annotation { "Feature Type Name" : "Feature", "Feature Type Description" : "" }
export const myFeature = defineFeature(function(context is Context, id is Id, definition is map)
    precondition{}
    {
        {
            var Q0;
            Q0=qCreatedBy(makeId("Top.planeOp"),FACE);
            var sketch = newSketch(context, id + "F0", { "sketchPlane" : qUnion([Q0])});
            skLineSegment(sketch, "E0.bottom", {"start": v(-41.2, 53) * mm, "end": v(24.8, 53) * mm});
            skLineSegment(sketch, "E0.top", {"start": v(-41.2, 0) * mm, "end": v(24.8, 0) * mm});
            skLineSegment(sketch, "E0.left", {"start": v(-44.2, 48.01) * mm, "end": v(-44.2, 15.01) * mm});
            skLineSegment(sketch, "E0.right", {"start": v(24.8, 53) * mm, "end": v(24.8, 0) * mm});
            skCircle(sketch, "E1", {"center": v(9.8, 2.5) * mm, "radius": 1.5 * mm});
            skCircle(sketch, "E2", {"center": v(9.8, 50.5) * mm, "radius": 1.5 * mm});
            skLineSegment(sketch, "E3", {"start": v(-41.2, 53) * mm, "end": v(-41.2, 50) * mm});
            skLineSegment(sketch, "E4", {"start": v(-41.2, 50) * mm, "end": v(-44.2, 48.01) * mm});
            skLineSegment(sketch, "E5", {"start": v(-44.2, 15.01) * mm, "end": v(-41.2, 13) * mm});
            skPoint(sketch, "E6.orphan", {"position": v(-44.2, 53) * mm});
            skLineSegment(sketch, "E7", {"start": v(-41.2, 12.57) * mm, "end": v(-41.2, 0) * mm});
            skPoint(sketch, "E8.orphan", {"position": v(-41.2, 0) * mm});
            skLineSegment(sketch, "E9.trimOffspring", {"start": v(-41.2, 13) * mm, "end": v(-41.2, 12.57) * mm});
            skCircle(sketch, "E10", {"center": v(-41.7, 17.47) * mm, "radius": 1.5 * mm});
            skPoint(sketch, "E11.centerSnap0", {"position": v(-41.2, 51.5) * mm});
            skLineSegment(sketch, "E12", {"start": v(-41.7, 17.47) * mm, "end": v(-41.7, 18.97) * mm});
            skLineSegment(sketch, "E13", {"start": v(-41.2, 47) * mm, "end": v(-41.2, 50) * mm});
            skCircle(sketch, "E14", {"center": v(-41.7, 45.53) * mm, "radius": 1.5 * mm});
            skLineSegment(sketch, "E15.bottom", {"start": v(13.3, 12) * mm, "end": v(27.3, 12) * mm});
            skLineSegment(sketch, "E15.top", {"start": v(13.3, 3) * mm, "end": v(27.3, 3) * mm});
            skLineSegment(sketch, "E15.left", {"start": v(13.3, 12) * mm, "end": v(13.3, 3) * mm});
            skLineSegment(sketch, "E15.right", {"start": v(27.3, 12) * mm, "end": v(27.3, 3) * mm});
            skSolve(sketch);
        }
        {
            var Q0;
            Q0=makeQuery(id+"F0.imprint","IMPRINT",FACE,{"disambiguationData":[TD([[makeQuery(id+"F0.imprint","IMPRINT",EDGE,{"derivedFrom":sQuery(id+"F0.wireOp",EDGE,"E0.bottom")}),-1.0]])]});
            var Q1;
            {var subQ5=sQuery(id+"F0.wireOp",EDGE,"E15.left");Q1=makeQuery(id+"F0.imprint","IMPRINT",FACE,{"disambiguationData":[TD([[makeQuery(id+"F0.imprint","IMPRINT",EDGE,{"derivedFrom":subQ5}),1.0]])]});}
            extrude(context, id + "F1", {"entities" : qUnion([Q0, Q1]), "depth" : 1.5 * mm});
        }
        {
            var Q0;
            Q0=makeQuery(id+"F1.opExtrude","CAP_FACE",FACE,{"disambiguationData":[OSD([sQuery(id+"F0.wireOp",EDGE,"E0.bottom"),sQuery(id+"F0.wireOp",EDGE,"E0.top"),sQuery(id+"F0.wireOp",EDGE,"E0.left"),sQuery(id+"F0.wireOp",EDGE,"E0.right"),sQuery(id+"F0.wireOp",EDGE,"E1"),sQuery(id+"F0.wireOp",EDGE,"E2"),sQuery(id+"F0.wireOp",EDGE,"E3"),sQuery(id+"F0.wireOp",EDGE,"E4"),sQuery(id+"F0.wireOp",EDGE,"E5"),sQuery(id+"F0.wireOp",EDGE,"E7"),sQuery(id+"F0.wireOp",EDGE,"E9.trimOffspring")])],"isStart":false});
            var sketch = newSketch(context, id + "F2", { "sketchPlane" : qUnion([Q0])});
            skLineSegment(sketch, "E16.bottom", {"start": v(-18.2, 51.5) * mm, "end": v(2.8, 51.5) * mm});
            skLineSegment(sketch, "E16.left", {"start": v(-18.2, 51.5) * mm, "end": v(-18.2, 49.5) * mm});
            skLineSegment(sketch, "E16.right", {"start": v(2.8, 51.5) * mm, "end": v(2.8, 49.5) * mm});
            skLineSegment(sketch, "E17", {"start": v(-18.2, 49.5) * mm, "end": v(2.8, 49.5) * mm});
            skLineSegment(sketch, "E18.bottom", {"start": v(-19.2, 49.5) * mm, "end": v(-40.2, 49.5) * mm});
            skLineSegment(sketch, "E18.top", {"start": v(-19.2, 51.5) * mm, "end": v(-40.2, 51.5) * mm});
            skLineSegment(sketch, "E18.left", {"start": v(-19.2, 49.5) * mm, "end": v(-19.2, 51.5) * mm});
            skLineSegment(sketch, "E18.right", {"start": v(-40.2, 49.5) * mm, "end": v(-40.2, 51.5) * mm});
            skLineSegment(sketch, "E19.bottom", {"start": v(-6.2, 1) * mm, "end": v(-22.2, 1) * mm});
            skLineSegment(sketch, "E19.top", {"start": v(-6.2, 3) * mm, "end": v(-22.2, 3) * mm});
            skLineSegment(sketch, "E19.left", {"start": v(-6.2, 1) * mm, "end": v(-6.2, 3) * mm});
            skLineSegment(sketch, "E19.right", {"start": v(-22.2, 1) * mm, "end": v(-22.2, 3) * mm});
            skLineSegment(sketch, "E20.bottom", {"start": v(-24.2, 1) * mm, "end": v(-40.2, 1) * mm});
            skLineSegment(sketch, "E20.top", {"start": v(-24.2, 3) * mm, "end": v(-40.2, 3) * mm});
            skLineSegment(sketch, "E20.left", {"start": v(-24.2, 1) * mm, "end": v(-24.2, 3) * mm});
            skLineSegment(sketch, "E20.right", {"start": v(-41.2, 1) * mm, "end": v(-41.2, 3) * mm});
            skLineSegment(sketch, "E21", {"start": v(-40.2, 3) * mm, "end": v(-40.2, 1) * mm});
            skSolve(sketch);
        }
        {
            var Q0;
            Q0 = qSketchRegion(id + "F2", true);
            extrude(context, id + "F3", {"entities" : qUnion([Q0]), "operationType" : NewBodyOperationType.ADD, "depth" : 9 * mm});
        }
        {
            var Q0;
            Q0=makeQuery(id+"F3.opExtrude","CAP_FACE",FACE,{"disambiguationData":[OSD([sQuery(id+"F2.wireOp",EDGE,"E18.bottom"),sQuery(id+"F2.wireOp",EDGE,"E18.top"),sQuery(id+"F2.wireOp",EDGE,"E18.left"),sQuery(id+"F2.wireOp",EDGE,"E18.right")])],"isStart":false});
            var sketch = newSketch(context, id + "F4", { "sketchPlane" : qUnion([Q0])});
            skLineSegment(sketch, "E22.bottom", {"start": v(-39.2, 51.25) * mm, "end": v(-37.7, 51.25) * mm});
            skLineSegment(sketch, "E22.top", {"start": v(-39.2, 49.75) * mm, "end": v(-37.7, 49.75) * mm});
            skLineSegment(sketch, "E22.left", {"start": v(-39.2, 51.25) * mm, "end": v(-39.2, 49.75) * mm});
            skLineSegment(sketch, "E22.right", {"start": v(-37.7, 51.25) * mm, "end": v(-37.7, 49.75) * mm});
            skLineSegment(sketch, "E23.bottom", {"start": v(-36.7, 51.25) * mm, "end": v(-35.2, 51.25) * mm});
            skLineSegment(sketch, "E23.top", {"start": v(-36.7, 49.75) * mm, "end": v(-35.2, 49.75) * mm});
            skLineSegment(sketch, "E23.left", {"start": v(-36.7, 51.25) * mm, "end": v(-36.7, 49.75) * mm});
            skLineSegment(sketch, "E23.right", {"start": v(-35.2, 51.25) * mm, "end": v(-35.2, 49.75) * mm});
            skLineSegment(sketch, "E24.bottom", {"start": v(-34.2, 51.25) * mm, "end": v(-32.7, 51.25) * mm});
            skLineSegment(sketch, "E24.top", {"start": v(-34.2, 49.75) * mm, "end": v(-32.7, 49.75) * mm});
            skLineSegment(sketch, "E24.left", {"start": v(-34.2, 51.25) * mm, "end": v(-34.2, 49.75) * mm});
            skLineSegment(sketch, "E24.right", {"start": v(-32.7, 51.25) * mm, "end": v(-32.7, 49.75) * mm});
            skLineSegment(sketch, "E25.bottom", {"start": v(-31.7, 51.25) * mm, "end": v(-30.2, 51.25) * mm});
            skLineSegment(sketch, "E25.top", {"start": v(-31.7, 49.75) * mm, "end": v(-30.2, 49.75) * mm});
            skLineSegment(sketch, "E25.left", {"start": v(-31.7, 51.25) * mm, "end": v(-31.7, 49.75) * mm});
            skLineSegment(sketch, "E25.right", {"start": v(-30.2, 51.25) * mm, "end": v(-30.2, 49.75) * mm});
            skLineSegment(sketch, "E26.bottom", {"start": v(-29.2, 51.25) * mm, "end": v(-27.7, 51.25) * mm});
            skLineSegment(sketch, "E26.top", {"start": v(-29.2, 49.75) * mm, "end": v(-27.7, 49.75) * mm});
            skLineSegment(sketch, "E26.left", {"start": v(-29.2, 51.25) * mm, "end": v(-29.2, 49.75) * mm});
            skLineSegment(sketch, "E26.right", {"start": v(-27.7, 51.25) * mm, "end": v(-27.7, 49.75) * mm});
            skLineSegment(sketch, "E27.bottom", {"start": v(-26.7, 51.25) * mm, "end": v(-25.2, 51.25) * mm});
            skLineSegment(sketch, "E27.top", {"start": v(-26.7, 49.75) * mm, "end": v(-25.2, 49.75) * mm});
            skLineSegment(sketch, "E27.left", {"start": v(-26.7, 51.25) * mm, "end": v(-26.7, 49.75) * mm});
            skLineSegment(sketch, "E27.right", {"start": v(-25.2, 51.25) * mm, "end": v(-25.2, 49.75) * mm});
            skLineSegment(sketch, "E28.right", {"start": v(124.56, 51.25) * mm, "end": v(124.56, 49.75) * mm});
            skLineSegment(sketch, "E29.bottom", {"start": v(-21.7, 51.25) * mm, "end": v(-20.2, 51.25) * mm});
            skLineSegment(sketch, "E29.top", {"start": v(-21.7, 49.75) * mm, "end": v(-20.2, 49.75) * mm});
            skLineSegment(sketch, "E29.left", {"start": v(-21.7, 51.25) * mm, "end": v(-21.7, 49.75) * mm});
            skLineSegment(sketch, "E29.right", {"start": v(-20.2, 51.25) * mm, "end": v(-20.2, 49.75) * mm});
            skLineSegment(sketch, "E30.bottom", {"start": v(-24.2, 51.25) * mm, "end": v(-22.7, 51.25) * mm});
            skLineSegment(sketch, "E30.top", {"start": v(-24.2, 49.75) * mm, "end": v(-22.7, 49.75) * mm});
            skLineSegment(sketch, "E30.left", {"start": v(-24.2, 51.25) * mm, "end": v(-24.2, 49.75) * mm});
            skLineSegment(sketch, "E30.right", {"start": v(-22.7, 51.25) * mm, "end": v(-22.7, 49.75) * mm});
            skSolve(sketch);
        }
        {
            var Q0;
            Q0 = qSketchRegion(id + "F4", true);
            extrude(context, id + "F5", {"entities" : qUnion([Q0]), "operationType" : NewBodyOperationType.REMOVE, "oppositeDirection" : true, "depth" : 6 * mm});
        }
        {
            var Q0;
            Q0=makeQuery(id+"F3.opExtrude","CAP_FACE",FACE,{"disambiguationData":[OSD([sQuery(id+"F2.wireOp",EDGE,"E16.bottom"),sQuery(id+"F2.wireOp",EDGE,"E16.left"),sQuery(id+"F2.wireOp",EDGE,"E16.right"),sQuery(id+"F2.wireOp",EDGE,"E17")])],"isStart":false});
            var sketch = newSketch(context, id + "F6", { "sketchPlane" : qUnion([Q0])});
            skLineSegment(sketch, "E31.bottom", {"start": v(-17.2, 51.25) * mm, "end": v(-15.7, 51.25) * mm});
            skLineSegment(sketch, "E31.top", {"start": v(-17.2, 49.75) * mm, "end": v(-15.7, 49.75) * mm});
            skLineSegment(sketch, "E31.left", {"start": v(-17.2, 51.25) * mm, "end": v(-17.2, 49.75) * mm});
            skLineSegment(sketch, "E31.right", {"start": v(-15.7, 51.25) * mm, "end": v(-15.7, 49.75) * mm});
            skLineSegment(sketch, "E32.bottom", {"start": v(-14.7, 51.25) * mm, "end": v(-13.2, 51.25) * mm});
            skLineSegment(sketch, "E32.top", {"start": v(-14.7, 49.75) * mm, "end": v(-13.2, 49.75) * mm});
            skLineSegment(sketch, "E32.left", {"start": v(-14.7, 51.25) * mm, "end": v(-14.7, 49.75) * mm});
            skLineSegment(sketch, "E32.right", {"start": v(-13.2, 51.25) * mm, "end": v(-13.2, 49.75) * mm});
            skLineSegment(sketch, "E33.bottom", {"start": v(-12.2, 51.25) * mm, "end": v(-10.7, 51.25) * mm});
            skLineSegment(sketch, "E33.top", {"start": v(-12.2, 49.75) * mm, "end": v(-10.7, 49.75) * mm});
            skLineSegment(sketch, "E33.left", {"start": v(-12.2, 51.25) * mm, "end": v(-12.2, 49.75) * mm});
            skLineSegment(sketch, "E33.right", {"start": v(-10.7, 51.25) * mm, "end": v(-10.7, 49.75) * mm});
            skLineSegment(sketch, "E34.bottom", {"start": v(-9.7, 51.25) * mm, "end": v(-8.2, 51.25) * mm});
            skLineSegment(sketch, "E34.top", {"start": v(-9.7, 49.75) * mm, "end": v(-8.2, 49.75) * mm});
            skLineSegment(sketch, "E34.left", {"start": v(-9.7, 51.25) * mm, "end": v(-9.7, 49.75) * mm});
            skLineSegment(sketch, "E34.right", {"start": v(-8.2, 51.25) * mm, "end": v(-8.2, 49.75) * mm});
            skLineSegment(sketch, "E35.bottom", {"start": v(-7.2, 51.25) * mm, "end": v(-5.7, 51.25) * mm});
            skLineSegment(sketch, "E35.top", {"start": v(-7.2, 49.75) * mm, "end": v(-5.7, 49.75) * mm});
            skLineSegment(sketch, "E35.left", {"start": v(-7.2, 51.25) * mm, "end": v(-7.2, 49.75) * mm});
            skLineSegment(sketch, "E35.right", {"start": v(-5.7, 51.25) * mm, "end": v(-5.7, 49.75) * mm});
            skLineSegment(sketch, "E36.bottom", {"start": v(-4.7, 51.25) * mm, "end": v(-3.2, 51.25) * mm});
            skLineSegment(sketch, "E36.top", {"start": v(-4.7, 49.75) * mm, "end": v(-3.2, 49.75) * mm});
            skLineSegment(sketch, "E36.left", {"start": v(-4.7, 51.25) * mm, "end": v(-4.7, 49.75) * mm});
            skLineSegment(sketch, "E36.right", {"start": v(-3.2, 51.25) * mm, "end": v(-3.2, 49.75) * mm});
            skLineSegment(sketch, "E37.right", {"start": v(137.9, 51.25) * mm, "end": v(137.9, 49.75) * mm});
            skLineSegment(sketch, "E38.bottom", {"start": v(0.3, 51.25) * mm, "end": v(1.8, 51.25) * mm});
            skLineSegment(sketch, "E38.top", {"start": v(0.3, 49.75) * mm, "end": v(1.8, 49.75) * mm});
            skLineSegment(sketch, "E38.left", {"start": v(0.3, 51.25) * mm, "end": v(0.3, 49.75) * mm});
            skLineSegment(sketch, "E38.right", {"start": v(1.8, 51.25) * mm, "end": v(1.8, 49.75) * mm});
            skLineSegment(sketch, "E39.bottom", {"start": v(-2.2, 51.25) * mm, "end": v(-0.7, 51.25) * mm});
            skLineSegment(sketch, "E39.top", {"start": v(-2.2, 49.75) * mm, "end": v(-0.7, 49.75) * mm});
            skLineSegment(sketch, "E39.left", {"start": v(-2.2, 51.25) * mm, "end": v(-2.2, 49.75) * mm});
            skLineSegment(sketch, "E39.right", {"start": v(-0.7, 51.25) * mm, "end": v(-0.7, 49.75) * mm});
            skSolve(sketch);
        }
        {
            var Q0;
            Q0=makeQuery(id+"F6.imprint","IMPRINT",FACE,{"disambiguationData":[TD([[makeQuery(id+"F6.imprint","IMPRINT",EDGE,{"derivedFrom":sQuery(id+"F6.wireOp",EDGE,"E32.bottom")}),-1.0]])]});
            var Q1;
            Q1=makeQuery(id+"F6.imprint","IMPRINT",FACE,{"disambiguationData":[TD([[makeQuery(id+"F6.imprint","IMPRINT",EDGE,{"derivedFrom":sQuery(id+"F6.wireOp",EDGE,"E33.bottom")}),-1.0]])]});
            var Q2;
            Q2=makeQuery(id+"F6.imprint","IMPRINT",FACE,{"disambiguationData":[TD([[makeQuery(id+"F6.imprint","IMPRINT",EDGE,{"derivedFrom":sQuery(id+"F6.wireOp",EDGE,"E34.bottom")}),-1.0]])]});
            var Q3;
            Q3=makeQuery(id+"F6.imprint","IMPRINT",FACE,{"disambiguationData":[TD([[makeQuery(id+"F6.imprint","IMPRINT",EDGE,{"derivedFrom":sQuery(id+"F6.wireOp",EDGE,"E35.bottom")}),-1.0]])]});
            var Q4;
            Q4=makeQuery(id+"F6.imprint","IMPRINT",FACE,{"disambiguationData":[TD([[makeQuery(id+"F6.imprint","IMPRINT",EDGE,{"derivedFrom":sQuery(id+"F6.wireOp",EDGE,"E36.bottom")}),-1.0]])]});
            var Q5;
            Q5=makeQuery(id+"F6.imprint","IMPRINT",FACE,{"disambiguationData":[TD([[makeQuery(id+"F6.imprint","IMPRINT",EDGE,{"derivedFrom":sQuery(id+"F6.wireOp",EDGE,"E38.bottom")}),-1.0]])]});
            var Q6;
            Q6=makeQuery(id+"F6.imprint","IMPRINT",FACE,{"disambiguationData":[TD([[makeQuery(id+"F6.imprint","IMPRINT",EDGE,{"derivedFrom":sQuery(id+"F6.wireOp",EDGE,"E39.bottom")}),-1.0]])]});
            var Q7;
            Q7=makeQuery(id+"F6.imprint","IMPRINT",FACE,{"disambiguationData":[TD([[makeQuery(id+"F6.imprint","IMPRINT",EDGE,{"derivedFrom":sQuery(id+"F6.wireOp",EDGE,"E31.bottom")}),-1.0]])]});
            var Q8;
            Q8=makeQuery(id+"F6.imprint","IMPRINT",FACE,{"disambiguationData":[TD([[makeQuery(id+"F6.imprint","IMPRINT",EDGE,{"derivedFrom":sQuery(id+"F6.wireOp",EDGE,"E32.bottom")}),-1.0]])]});
            var Q9;
            Q9=makeQuery(id+"F6.imprint","IMPRINT",FACE,{"disambiguationData":[TD([[makeQuery(id+"F6.imprint","IMPRINT",EDGE,{"derivedFrom":sQuery(id+"F6.wireOp",EDGE,"E33.bottom")}),-1.0]])]});
            var Q10;
            Q10=makeQuery(id+"F6.imprint","IMPRINT",FACE,{"disambiguationData":[TD([[makeQuery(id+"F6.imprint","IMPRINT",EDGE,{"derivedFrom":sQuery(id+"F6.wireOp",EDGE,"E34.bottom")}),-1.0]])]});
            var Q11;
            Q11=makeQuery(id+"F6.imprint","IMPRINT",FACE,{"disambiguationData":[TD([[makeQuery(id+"F6.imprint","IMPRINT",EDGE,{"derivedFrom":sQuery(id+"F6.wireOp",EDGE,"E35.bottom")}),-1.0]])]});
            var Q12;
            Q12=makeQuery(id+"F6.imprint","IMPRINT",FACE,{"disambiguationData":[TD([[makeQuery(id+"F6.imprint","IMPRINT",EDGE,{"derivedFrom":sQuery(id+"F6.wireOp",EDGE,"E36.bottom")}),-1.0]])]});
            var Q13;
            Q13=makeQuery(id+"F6.imprint","IMPRINT",FACE,{"disambiguationData":[TD([[makeQuery(id+"F6.imprint","IMPRINT",EDGE,{"derivedFrom":sQuery(id+"F6.wireOp",EDGE,"E38.bottom")}),-1.0]])]});
            var Q14;
            Q14=makeQuery(id+"F6.imprint","IMPRINT",FACE,{"disambiguationData":[TD([[makeQuery(id+"F6.imprint","IMPRINT",EDGE,{"derivedFrom":sQuery(id+"F6.wireOp",EDGE,"E39.bottom")}),-1.0]])]});
            extrude(context, id + "F7", {"entities" : qUnion([Q0, Q1, Q2, Q3, Q4, Q5, Q6, Q7, Q8, Q9, Q10, Q11, Q12, Q13, Q14]), "operationType" : NewBodyOperationType.REMOVE, "oppositeDirection" : true, "depth" : 6 * mm});
        }
        {
            var Q0;
            Q0=makeQuery(id+"F3.opExtrude","CAP_FACE",FACE,{"disambiguationData":[OSD([sQuery(id+"F2.wireOp",EDGE,"E20.bottom"),sQuery(id+"F2.wireOp",EDGE,"E20.top"),sQuery(id+"F2.wireOp",EDGE,"E20.left"),sQuery(id+"F2.wireOp",EDGE,"E21")])],"isStart":false});
            var sketch = newSketch(context, id + "F8", { "sketchPlane" : qUnion([Q0])});
            skLineSegment(sketch, "E40.bottom", {"start": v(-39.2, 2.75) * mm, "end": v(-37.7, 2.75) * mm});
            skLineSegment(sketch, "E40.top", {"start": v(-39.2, 1.25) * mm, "end": v(-37.7, 1.25) * mm});
            skLineSegment(sketch, "E40.left", {"start": v(-39.2, 2.75) * mm, "end": v(-39.2, 1.25) * mm});
            skLineSegment(sketch, "E40.right", {"start": v(-37.7, 2.75) * mm, "end": v(-37.7, 1.25) * mm});
            skLineSegment(sketch, "E41.bottom", {"start": v(-36.7, 2.75) * mm, "end": v(-35.2, 2.75) * mm});
            skLineSegment(sketch, "E41.top", {"start": v(-36.7, 1.25) * mm, "end": v(-35.2, 1.25) * mm});
            skLineSegment(sketch, "E41.left", {"start": v(-36.7, 2.75) * mm, "end": v(-36.7, 1.25) * mm});
            skLineSegment(sketch, "E41.right", {"start": v(-35.2, 2.75) * mm, "end": v(-35.2, 1.25) * mm});
            skLineSegment(sketch, "E42.bottom", {"start": v(-34.2, 2.75) * mm, "end": v(-32.7, 2.75) * mm});
            skLineSegment(sketch, "E42.top", {"start": v(-34.2, 1.25) * mm, "end": v(-32.7, 1.25) * mm});
            skLineSegment(sketch, "E42.left", {"start": v(-34.2, 2.75) * mm, "end": v(-34.2, 1.25) * mm});
            skLineSegment(sketch, "E42.right", {"start": v(-32.7, 2.75) * mm, "end": v(-32.7, 1.25) * mm});
            skLineSegment(sketch, "E43.bottom", {"start": v(-31.7, 2.75) * mm, "end": v(-30.2, 2.75) * mm});
            skLineSegment(sketch, "E43.top", {"start": v(-31.7, 1.25) * mm, "end": v(-30.2, 1.25) * mm});
            skLineSegment(sketch, "E43.left", {"start": v(-31.7, 2.75) * mm, "end": v(-31.7, 1.25) * mm});
            skLineSegment(sketch, "E43.right", {"start": v(-30.2, 2.75) * mm, "end": v(-30.2, 1.25) * mm});
            skLineSegment(sketch, "E44.bottom", {"start": v(-29.2, 2.75) * mm, "end": v(-27.7, 2.75) * mm});
            skLineSegment(sketch, "E44.top", {"start": v(-29.2, 1.25) * mm, "end": v(-27.7, 1.25) * mm});
            skLineSegment(sketch, "E44.left", {"start": v(-29.2, 2.75) * mm, "end": v(-29.2, 1.25) * mm});
            skLineSegment(sketch, "E44.right", {"start": v(-27.7, 2.75) * mm, "end": v(-27.7, 1.25) * mm});
            skLineSegment(sketch, "E45.bottom", {"start": v(-26.7, 2.75) * mm, "end": v(-25.2, 2.75) * mm});
            skLineSegment(sketch, "E45.top", {"start": v(-26.7, 1.25) * mm, "end": v(-25.2, 1.25) * mm});
            skLineSegment(sketch, "E45.left", {"start": v(-26.7, 2.75) * mm, "end": v(-26.7, 1.25) * mm});
            skLineSegment(sketch, "E45.right", {"start": v(-25.2, 2.75) * mm, "end": v(-25.2, 1.25) * mm});
            skLineSegment(sketch, "E46.right", {"start": v(102.2, 2.75) * mm, "end": v(102.2, 1.25) * mm});
            skSolve(sketch);
        }
        {
            var Q0;
            Q0 = qSketchRegion(id + "F8", true);
            extrude(context, id + "F9", {"entities" : qUnion([Q0]), "operationType" : NewBodyOperationType.REMOVE, "oppositeDirection" : true, "depth" : 6 * mm});
        }
        {
            var Q0;
            Q0=makeQuery(id+"F3.opExtrude","CAP_FACE",FACE,{"disambiguationData":[OSD([sQuery(id+"F2.wireOp",EDGE,"E19.bottom"),sQuery(id+"F2.wireOp",EDGE,"E19.top"),sQuery(id+"F2.wireOp",EDGE,"E19.left"),sQuery(id+"F2.wireOp",EDGE,"E19.right")])],"isStart":false});
            var sketch = newSketch(context, id + "F10", { "sketchPlane" : qUnion([Q0])});
            skLineSegment(sketch, "E47.bottom", {"start": v(-21.2, 2.75) * mm, "end": v(-19.7, 2.75) * mm});
            skLineSegment(sketch, "E47.top", {"start": v(-21.2, 1.25) * mm, "end": v(-19.7, 1.25) * mm});
            skLineSegment(sketch, "E47.left", {"start": v(-21.2, 2.75) * mm, "end": v(-21.2, 1.25) * mm});
            skLineSegment(sketch, "E47.right", {"start": v(-19.7, 2.75) * mm, "end": v(-19.7, 1.25) * mm});
            skLineSegment(sketch, "E48.bottom", {"start": v(-18.7, 2.75) * mm, "end": v(-17.2, 2.75) * mm});
            skLineSegment(sketch, "E48.top", {"start": v(-18.7, 1.25) * mm, "end": v(-17.2, 1.25) * mm});
            skLineSegment(sketch, "E48.left", {"start": v(-18.7, 2.75) * mm, "end": v(-18.7, 1.25) * mm});
            skLineSegment(sketch, "E48.right", {"start": v(-17.2, 2.75) * mm, "end": v(-17.2, 1.25) * mm});
            skLineSegment(sketch, "E49.bottom", {"start": v(-16.2, 2.75) * mm, "end": v(-14.7, 2.75) * mm});
            skLineSegment(sketch, "E49.top", {"start": v(-16.2, 1.25) * mm, "end": v(-14.7, 1.25) * mm});
            skLineSegment(sketch, "E49.left", {"start": v(-16.2, 2.75) * mm, "end": v(-16.2, 1.25) * mm});
            skLineSegment(sketch, "E49.right", {"start": v(-14.7, 2.75) * mm, "end": v(-14.7, 1.25) * mm});
            skLineSegment(sketch, "E50.bottom", {"start": v(-13.7, 2.75) * mm, "end": v(-12.2, 2.75) * mm});
            skLineSegment(sketch, "E50.top", {"start": v(-13.7, 1.25) * mm, "end": v(-12.2, 1.25) * mm});
            skLineSegment(sketch, "E50.left", {"start": v(-13.7, 2.75) * mm, "end": v(-13.7, 1.25) * mm});
            skLineSegment(sketch, "E50.right", {"start": v(-12.2, 2.75) * mm, "end": v(-12.2, 1.25) * mm});
            skLineSegment(sketch, "E51.bottom", {"start": v(-11.2, 2.75) * mm, "end": v(-9.7, 2.75) * mm});
            skLineSegment(sketch, "E51.top", {"start": v(-11.2, 1.25) * mm, "end": v(-9.7, 1.25) * mm});
            skLineSegment(sketch, "E51.left", {"start": v(-11.2, 2.75) * mm, "end": v(-11.2, 1.25) * mm});
            skLineSegment(sketch, "E51.right", {"start": v(-9.7, 2.75) * mm, "end": v(-9.7, 1.25) * mm});
            skLineSegment(sketch, "E52.bottom", {"start": v(-8.7, 2.75) * mm, "end": v(-7.2, 2.75) * mm});
            skLineSegment(sketch, "E52.top", {"start": v(-8.7, 1.25) * mm, "end": v(-7.2, 1.25) * mm});
            skLineSegment(sketch, "E52.left", {"start": v(-8.7, 2.75) * mm, "end": v(-8.7, 1.25) * mm});
            skLineSegment(sketch, "E52.right", {"start": v(-7.2, 2.75) * mm, "end": v(-7.2, 1.25) * mm});
            skLineSegment(sketch, "E53.right", {"start": v(106.92, 2.75) * mm, "end": v(106.92, 1.25) * mm});
            skSolve(sketch);
        }
        {
            var Q0;
            Q0=makeQuery(id+"F10.imprint","IMPRINT",FACE,{"disambiguationData":[TD([[makeQuery(id+"F10.imprint","IMPRINT",EDGE,{"derivedFrom":sQuery(id+"F10.wireOp",EDGE,"E47.bottom")}),-1.0]])]});
            var Q1;
            Q1=makeQuery(id+"F10.imprint","IMPRINT",FACE,{"disambiguationData":[TD([[makeQuery(id+"F10.imprint","IMPRINT",EDGE,{"derivedFrom":sQuery(id+"F10.wireOp",EDGE,"E48.bottom")}),-1.0]])]});
            var Q2;
            Q2=makeQuery(id+"F10.imprint","IMPRINT",FACE,{"disambiguationData":[TD([[makeQuery(id+"F10.imprint","IMPRINT",EDGE,{"derivedFrom":sQuery(id+"F10.wireOp",EDGE,"E49.bottom")}),-1.0]])]});
            var Q3;
            Q3=makeQuery(id+"F10.imprint","IMPRINT",FACE,{"disambiguationData":[TD([[makeQuery(id+"F10.imprint","IMPRINT",EDGE,{"derivedFrom":sQuery(id+"F10.wireOp",EDGE,"E50.bottom")}),-1.0]])]});
            var Q4;
            Q4=makeQuery(id+"F10.imprint","IMPRINT",FACE,{"disambiguationData":[TD([[makeQuery(id+"F10.imprint","IMPRINT",EDGE,{"derivedFrom":sQuery(id+"F10.wireOp",EDGE,"E51.bottom")}),-1.0]])]});
            var Q5;
            Q5=makeQuery(id+"F10.imprint","IMPRINT",FACE,{"disambiguationData":[TD([[makeQuery(id+"F10.imprint","IMPRINT",EDGE,{"derivedFrom":sQuery(id+"F10.wireOp",EDGE,"E52.bottom")}),-1.0]])]});
            extrude(context, id + "F11", {"entities" : qUnion([Q0, Q1, Q2, Q3, Q4, Q5]), "operationType" : NewBodyOperationType.REMOVE, "oppositeDirection" : true, "depth" : 6 * mm});
        }
        {
            var Q0;
            Q0=makeQuery(id+"F1.opExtrude","CAP_FACE",FACE,{"disambiguationData":[OSD([sQuery(id+"F0.wireOp",EDGE,"E0.bottom"),sQuery(id+"F0.wireOp",EDGE,"E0.top"),sQuery(id+"F0.wireOp",EDGE,"E0.left"),sQuery(id+"F0.wireOp",EDGE,"E0.right"),sQuery(id+"F0.wireOp",EDGE,"E1"),sQuery(id+"F0.wireOp",EDGE,"E2"),sQuery(id+"F0.wireOp",EDGE,"E3"),sQuery(id+"F0.wireOp",EDGE,"E4"),sQuery(id+"F0.wireOp",EDGE,"E5"),sQuery(id+"F0.wireOp",EDGE,"E7"),sQuery(id+"F0.wireOp",EDGE,"E9.trimOffspring"),sQuery(id+"F0.wireOp",EDGE,"E10"),sQuery(id+"F0.wireOp",EDGE,"E14")])],"isStart":false});
            var sketch = newSketch(context, id + "F12", { "sketchPlane" : qUnion([Q0])});
            skLineSegment(sketch, "E54.bottom", {"start": v(2.3, 8) * mm, "end": v(5.3, 8) * mm});
            skLineSegment(sketch, "E54.top", {"start": v(0.8, 2) * mm, "end": v(6.8, 2) * mm});
            skLineSegment(sketch, "E54.left", {"start": v(0.8, 6.5) * mm, "end": v(0.8, 2) * mm});
            skLineSegment(sketch, "E54.right", {"start": v(6.8, 6.5) * mm, "end": v(6.8, 2) * mm});
            skPoint(sketch, "E55.oppositeSnap0", {"position": v(-6.2, 2) * mm});
            skLineSegment(sketch, "E55.bottom", {"start": v(-1, 8) * mm, "end": v(-4, 8) * mm});
            skLineSegment(sketch, "E55.top", {"start": v(0.5, 2) * mm, "end": v(-5.5, 2) * mm});
            skLineSegment(sketch, "E55.left", {"start": v(0.5, 6.5) * mm, "end": v(0.5, 2) * mm});
            skLineSegment(sketch, "E55.right", {"start": v(-5.5, 6.5) * mm, "end": v(-5.5, 2) * mm});
            skLineSegment(sketch, "E56", {"start": v(-4, 8) * mm, "end": v(-5.5, 6.5) * mm});
            skLineSegment(sketch, "E57", {"start": v(-1, 8) * mm, "end": v(0.5, 6.5) * mm});
            skLineSegment(sketch, "E58", {"start": v(2.3, 8) * mm, "end": v(0.8, 6.5) * mm});
            skLineSegment(sketch, "E59", {"start": v(5.3, 8) * mm, "end": v(6.8, 6.5) * mm});
            skPoint(sketch, "E60.orphan", {"position": v(-5.5, 8) * mm});
            skPoint(sketch, "E61.orphan", {"position": v(0.5, 8) * mm});
            skPoint(sketch, "E62.orphan", {"position": v(0.8, 8) * mm});
            skPoint(sketch, "E63.orphan", {"position": v(6.8, 8) * mm});
            skSolve(sketch);
        }
        {
            var Q0;
            Q0 = qSketchRegion(id + "F12", true);
            extrude(context, id + "F13", {"entities" : qUnion([Q0]), "operationType" : NewBodyOperationType.ADD, "depth" : 1.5 * mm});
        }
        {
            var Q0;
            Q0=makeQuery(id+"F13.opExtrude","CAP_FACE",FACE,{"disambiguationData":[OSD([sQuery(id+"F12.wireOp",EDGE,"E55.bottom"),sQuery(id+"F12.wireOp",EDGE,"E55.top"),sQuery(id+"F12.wireOp",EDGE,"E55.left"),sQuery(id+"F12.wireOp",EDGE,"E55.right"),sQuery(id+"F12.wireOp",EDGE,"E56"),sQuery(id+"F12.wireOp",EDGE,"E57")])],"isStart":false});
            var sketch = newSketch(context, id + "F14", { "sketchPlane" : qUnion([Q0])});
            skCircle(sketch, "E64", {"center": v(-2.5, 5) * mm, "radius": 2.85 * mm});
            skPoint(sketch, "E64.centerSnap0", {"position": v(-2.5, 8) * mm});
            skSolve(sketch);
        }
        {
            var Q0;
            Q0=makeQuery(id+"F13.opExtrude","CAP_FACE",FACE,{"disambiguationData":[OSD([sQuery(id+"F12.wireOp",EDGE,"E54.bottom"),sQuery(id+"F12.wireOp",EDGE,"E54.top"),sQuery(id+"F12.wireOp",EDGE,"E54.left"),sQuery(id+"F12.wireOp",EDGE,"E54.right"),sQuery(id+"F12.wireOp",EDGE,"E58"),sQuery(id+"F12.wireOp",EDGE,"E59")])],"isStart":false});
            var sketch = newSketch(context, id + "F15", { "sketchPlane" : qUnion([Q0])});
            skCircle(sketch, "E65", {"center": v(3.8, 5) * mm, "radius": 2.85 * mm});
            skPoint(sketch, "E65.centerSnap0", {"position": v(3.8, 8) * mm});
            skSolve(sketch);
        }
        {
            var Q0;
            Q0=makeQuery(id+"F15.imprint","IMPRINT",FACE,{"disambiguationData":[TD([[makeQuery(id+"F15.imprint","IMPRINT",EDGE,{"derivedFrom":sQuery(id+"F15.wireOp",EDGE,"E65")}),1.0]])]});
            var Q1;
            Q1=makeQuery(id+"F14.imprint","IMPRINT",FACE,{"disambiguationData":[TD([[makeQuery(id+"F14.imprint","IMPRINT",EDGE,{"derivedFrom":sQuery(id+"F14.wireOp",EDGE,"E64")}),1.0]])]});
            extrude(context, id + "F16", {"entities" : qUnion([Q0, Q1]), "operationType" : NewBodyOperationType.ADD, "depth" : 6.5 * mm});
        }
        {
            var Q0;
            Q0=makeQuery(id+"F1.opExtrude","CAP_FACE",FACE,{"disambiguationData":[OSD([sQuery(id+"F0.wireOp",EDGE,"E0.bottom"),sQuery(id+"F0.wireOp",EDGE,"E0.top"),sQuery(id+"F0.wireOp",EDGE,"E0.left"),sQuery(id+"F0.wireOp",EDGE,"E0.right"),sQuery(id+"F0.wireOp",EDGE,"E1"),sQuery(id+"F0.wireOp",EDGE,"E2"),sQuery(id+"F0.wireOp",EDGE,"E3"),sQuery(id+"F0.wireOp",EDGE,"E4"),sQuery(id+"F0.wireOp",EDGE,"E5"),sQuery(id+"F0.wireOp",EDGE,"E7"),sQuery(id+"F0.wireOp",EDGE,"E9.trimOffspring"),sQuery(id+"F0.wireOp",EDGE,"E10"),sQuery(id+"F0.wireOp",EDGE,"E14")])],"isStart":false});
            var sketch = newSketch(context, id + "F17", { "sketchPlane" : qUnion([Q0])});
            skLineSegment(sketch, "E66.bottom", {"start": v(13.3, 12) * mm, "end": v(27.3, 12) * mm});
            skLineSegment(sketch, "E66.top", {"start": v(13.3, 3) * mm, "end": v(27.3, 3) * mm});
            skLineSegment(sketch, "E66.left", {"start": v(13.3, 12) * mm, "end": v(13.3, 3) * mm});
            skLineSegment(sketch, "E66.right", {"start": v(27.3, 12) * mm, "end": v(27.3, 3) * mm});
            skSolve(sketch);
        }
        {
            var Q0;
            Q0 = qSketchRegion(id + "F17", true);
            extrude(context, id + "F18", {"entities" : qUnion([Q0]), "operationType" : NewBodyOperationType.ADD, "depth" : 11 * mm});
        }
        {
            var Q0;
            Q0=makeQuery(id+"F18.opExtrude","SWEPT_FACE",FACE,{"disambiguationData":[OSD([sQuery(id+"F17.wireOp",EDGE,"E66.left")])]});
            var sketch = newSketch(context, id + "F19", { "sketchPlane" : qUnion([Q0])});
            skLineSegment(sketch, "E67", {"start": v(-11.7, 8) * mm, "end": v(-11.7, 1.5) * mm});
            skLineSegment(sketch, "E68", {"start": v(-3.3, 8) * mm, "end": v(-3.3, 1.5) * mm});
            skLineSegment(sketch, "E69", {"start": v(-11.7, 8) * mm, "end": v(-3.3, 8) * mm});
            skPoint(sketch, "E69.endSnap0", {"position": v(-3.3, 7) * mm});
            skCircle(sketch, "E70", {"center": v(-7.5, 8) * mm, "radius": 4.2 * mm});
            skLineSegment(sketch, "E71", {"start": v(-11.7, 8) * mm, "end": v(-12, 8) * mm});
            skLineSegment(sketch, "E72", {"start": v(-12, 8) * mm, "end": v(-3, 8) * mm});
            skPoint(sketch, "E73.orphan", {"position": v(-11.7, 12.5) * mm});
            skPoint(sketch, "E74.orphan", {"position": v(-3.3, 12.5) * mm});
            skSolve(sketch);
        }
        {
            var Q0;
            {var subQ0=sQuery(id+"F19.wireOp",EDGE,"E67");var subQ1=makeQuery(id+"F18.opExtrude","CAP_EDGE",EDGE,{"disambiguationData":[OSD([sQuery(id+"F17.wireOp",EDGE,"E66.left")])],"isStart":false});var subQ2=makeQuery(id+"F19.imprint","INTERSECT",VERTEX,{"derivedFrom":[subQ1,subQ0]});Q0=makeQuery(id+"F19.imprint","IMPRINT",FACE,{"disambiguationData":[TD([[makeQuery(id+"F19.imprint","IMPRINT",EDGE,{"disambiguationData":[TD([[subQ2,-1.0]])],"derivedFrom":subQ1}),-1.0]])]});}
            extrude(context, id + "F20", {"entities" : qUnion([Q0]), "operationType" : NewBodyOperationType.REMOVE, "oppositeDirection" : true, "depth" : 10 * mm});
        }
        {
            var Q0;
            Q0=makeQuery(id+"F18.opExtrude","SWEPT_FACE",FACE,{"disambiguationData":[OSD([sQuery(id+"F17.wireOp",EDGE,"E66.right")])]});
            var sketch = newSketch(context, id + "F21", { "sketchPlane" : qUnion([Q0])});
            skCircle(sketch, "E75", {"center": v(7.5, 7.5) * mm, "radius": 3 * mm});
            skSolve(sketch);
        }
        {
            var Q0;
            Q0 = qSketchRegion(id + "F21", true);
            extrude(context, id + "F22", {"entities" : qUnion([Q0]), "operationType" : NewBodyOperationType.REMOVE, "oppositeDirection" : true, "depth" : 12.5 * mm});
        }
        {
            var Q0;
            Q0=makeQuery(id+"F1.opExtrude","CAP_FACE",FACE,{"disambiguationData":[OSD([sQuery(id+"F0.wireOp",EDGE,"E0.bottom"),sQuery(id+"F0.wireOp",EDGE,"E0.top"),sQuery(id+"F0.wireOp",EDGE,"E0.left"),sQuery(id+"F0.wireOp",EDGE,"E0.right"),sQuery(id+"F0.wireOp",EDGE,"E1"),sQuery(id+"F0.wireOp",EDGE,"E2"),sQuery(id+"F0.wireOp",EDGE,"E3"),sQuery(id+"F0.wireOp",EDGE,"E4"),sQuery(id+"F0.wireOp",EDGE,"E5"),sQuery(id+"F0.wireOp",EDGE,"E7"),sQuery(id+"F0.wireOp",EDGE,"E9.trimOffspring"),sQuery(id+"F0.wireOp",EDGE,"E10"),sQuery(id+"F0.wireOp",EDGE,"E14")])],"isStart":false});
            var sketch = newSketch(context, id + "F23", { "sketchPlane" : qUnion([Q0])});
            skLineSegment(sketch, "E76.bottom", {"start": v(18.3, 46) * mm, "end": v(27.3, 46) * mm});
            skLineSegment(sketch, "E76.top", {"start": v(18.3, 39) * mm, "end": v(27.3, 39) * mm});
            skLineSegment(sketch, "E76.left", {"start": v(18.3, 46) * mm, "end": v(18.3, 39) * mm});
            skLineSegment(sketch, "E76.right", {"start": v(27.3, 46) * mm, "end": v(27.3, 39) * mm});
            skSolve(sketch);
        }
        {
            var Q0;
            {var subQ0=sQuery(id+"F23.wireOp",EDGE,"E76.left");Q0=makeQuery(id+"F23.imprint","IMPRINT",FACE,{"disambiguationData":[TD([[makeQuery(id+"F23.imprint","IMPRINT",EDGE,{"derivedFrom":subQ0}),1.0]])]});}
            var Q1;
            {var subQ0=sQuery(id+"F23.wireOp",EDGE,"E76.right");Q1=makeQuery(id+"F23.imprint","IMPRINT",FACE,{"disambiguationData":[TD([[makeQuery(id+"F23.imprint","IMPRINT",EDGE,{"derivedFrom":subQ0}),-1.0]])]});}
            extrude(context, id + "F24", {"entities" : qUnion([Q0, Q1]), "operationType" : NewBodyOperationType.ADD, "depth" : 4 * mm});
        }
        {
            var Q0;
            Q0=makeQuery(id+"F24.opExtrude","SWEPT_FACE",FACE,{"disambiguationData":[OSD([sQuery(id+"F23.wireOp",EDGE,"E76.right")])]});
            var sketch = newSketch(context, id + "F25", { "sketchPlane" : qUnion([Q0])});
            skLineSegment(sketch, "E77", {"start": v(39, 3.5) * mm, "end": v(39.5, 3.5) * mm});
            skLineSegment(sketch, "E78", {"start": v(46, 3.5) * mm, "end": v(45.28, 3.5) * mm});
            skLineSegment(sketch, "E79", {"start": v(45.28, 3.5) * mm, "end": v(45.28, 1.5) * mm});
            skLineSegment(sketch, "E80", {"start": v(39.5, 3.5) * mm, "end": v(39.5, 1.5) * mm});
            skArc(sketch, "E81", {"start": v(39.5, 3.35) * mm, "mid": v(39.43, 3.43) * mm, "end": v(39.35, 3.5) * mm});
            skArc(sketch, "E82", {"start": v(45.43, 3.5) * mm, "mid": v(45.36, 3.43) * mm, "end": v(45.28, 3.35) * mm});
            skSolve(sketch);
        }
        {
            var Q0;
            {var subQ6=sQuery(id+"F25.wireOp",EDGE,"E81");Q0=makeQuery(id+"F25.imprint","IMPRINT",FACE,{"disambiguationData":[TD([[makeQuery(id+"F25.imprint","IMPRINT",EDGE,{"derivedFrom":subQ6}),1.0]])]});}
            var Q1;
            {var subQ6=sQuery(id+"F25.wireOp",EDGE,"E82");Q1=makeQuery(id+"F25.imprint","IMPRINT",FACE,{"disambiguationData":[TD([[makeQuery(id+"F25.imprint","IMPRINT",EDGE,{"derivedFrom":subQ6}),1.0]])]});}
            extrude(context, id + "F26", {"entities" : qUnion([Q0, Q1]), "operationType" : NewBodyOperationType.REMOVE, "oppositeDirection" : true, "depth" : 10 * mm});
        }
        {
            var Q0;
            Q0=makeQuery(id+"F24.opExtrude","SWEPT_FACE",FACE,{"disambiguationData":[OSD([sQuery(id+"F23.wireOp",EDGE,"E76.right")])]});
            var sketch = newSketch(context, id + "F27", { "sketchPlane" : qUnion([Q0])});
            skPoint(sketch, "E83.oppositeSnap0", {"position": v(45.72, 3.5) * mm});
            skPoint(sketch, "E83.right.end.orphan", {"position": v(45.72, 3.94) * mm});
            skLineSegment(sketch, "E84.bottom", {"start": v(39.2, 5.3) * mm, "end": v(45.8, 5.3) * mm});
            skLineSegment(sketch, "E84.top", {"start": v(39.2, 3.7) * mm, "end": v(39.35, 3.7) * mm});
            skLineSegment(sketch, "E84.left", {"start": v(39.2, 5.3) * mm, "end": v(39.2, 3.7) * mm});
            skLineSegment(sketch, "E84.right", {"start": v(45.8, 5.3) * mm, "end": v(45.8, 3.7) * mm});
            skLineSegment(sketch, "E85.top", {"start": v(39.75, 1.7) * mm, "end": v(45.08, 1.7) * mm});
            skLineSegment(sketch, "E85.left", {"start": v(39.75, 3.35) * mm, "end": v(39.75, 1.7) * mm});
            skLineSegment(sketch, "E85.right", {"start": v(45.08, 3.35) * mm, "end": v(45.08, 1.7) * mm});
            skArc(sketch, "E86", {"start": v(45.43, 3.7) * mm, "mid": v(45.19, 3.6) * mm, "end": v(45.08, 3.35) * mm});
            skLineSegment(sketch, "E87.trimOffspring", {"start": v(45.43, 3.7) * mm, "end": v(45.8, 3.7) * mm});
            skArc(sketch, "E88", {"start": v(39.75, 3.35) * mm, "mid": v(39.62, 3.6) * mm, "end": v(39.35, 3.7) * mm});
            skPoint(sketch, "E89.end.orphan", {"position": v(39.75, 3.7) * mm});
            skSolve(sketch);
        }
        {
            var Q0;
            Q0=makeQuery(id+"F27.imprint","IMPRINT",FACE,{"disambiguationData":[TD([[makeQuery(id+"F27.imprint","IMPRINT",EDGE,{"derivedFrom":sQuery(id+"F27.wireOp",EDGE,"E84.bottom")}),-1.0]])]});
            extrude(context, id + "F28", {"entities" : qUnion([Q0]), "operationType" : NewBodyOperationType.REMOVE, "oppositeDirection" : true, "depth" : 7.5 * mm});
        }
        {
            var Q0;
            {var subQ0=sQuery(id+"F23.wireOp",EDGE,"E76.right");var subQ1=makeQuery(id+"F24.opExtrude","CAP_EDGE",EDGE,{"disambiguationData":[OSD([subQ0])],"isStart":true});Q0=makeQuery(id+"F26.boolean.opBoolean","MERGE",FACE,{"derivedFrom":[makeQuery(id+"F1.opExtrude","CAP_FACE",FACE,{"disambiguationData":[OSD([sQuery(id+"F0.wireOp",EDGE,"E0.bottom"),sQuery(id+"F0.wireOp",EDGE,"E0.top"),sQuery(id+"F0.wireOp",EDGE,"E0.left"),sQuery(id+"F0.wireOp",EDGE,"E0.right"),sQuery(id+"F0.wireOp",EDGE,"E1"),sQuery(id+"F0.wireOp",EDGE,"E2"),sQuery(id+"F0.wireOp",EDGE,"E3"),sQuery(id+"F0.wireOp",EDGE,"E4"),sQuery(id+"F0.wireOp",EDGE,"E5"),sQuery(id+"F0.wireOp",EDGE,"E7"),sQuery(id+"F0.wireOp",EDGE,"E9.trimOffspring"),sQuery(id+"F0.wireOp",EDGE,"E10"),sQuery(id+"F0.wireOp",EDGE,"E14")])],"isStart":false}),makeQuery(id+"F26.opExtrude","SWEPT_FACE",FACE,{"disambiguationData":[OSD([subQ0]),TDD([makeQuery(id+"F25.imprint","IMPRINT",EDGE,{"disambiguationData":[TD([[makeQuery(id+"F25.imprint","INTERSECT",VERTEX,{"derivedFrom":[subQ1,sQuery(id+"F25.wireOp",EDGE,"E79")]}),1.0]])],"derivedFrom":subQ1})])]}),makeQuery(id+"F26.opExtrude","SWEPT_FACE",FACE,{"disambiguationData":[OSD([subQ0]),TDD([makeQuery(id+"F25.imprint","IMPRINT",EDGE,{"disambiguationData":[TD([[makeQuery(id+"F25.imprint","INTERSECT",VERTEX,{"derivedFrom":[subQ1,sQuery(id+"F25.wireOp",EDGE,"E80")]}),-1.0]])],"derivedFrom":subQ1})])]})]});}
            var sketch = newSketch(context, id + "F29", { "sketchPlane" : qUnion([Q0])});
            skLineSegment(sketch, "E90.bottom", {"start": v(-39.7, 20) * mm, "end": v(-4.7, 20) * mm});
            skLineSegment(sketch, "E90.top", {"start": v(-39.7, 11) * mm, "end": v(-4.7, 11) * mm});
            skLineSegment(sketch, "E90.left", {"start": v(-39.7, 20) * mm, "end": v(-39.7, 11) * mm});
            skLineSegment(sketch, "E90.right", {"start": v(-4.7, 20) * mm, "end": v(-4.7, 11) * mm});
            skSolve(sketch);
        }
        {
            var Q0;
            Q0=makeQuery(id+"F29.imprint","IMPRINT",FACE,{"disambiguationData":[TD([[makeQuery(id+"F29.imprint","IMPRINT",EDGE,{"derivedFrom":sQuery(id+"F29.wireOp",EDGE,"E90.bottom")}),-1.0]])]});
            extrude(context, id + "F30", {"entities" : qUnion([Q0]), "operationType" : NewBodyOperationType.ADD, "depth" : 5 * mm});
        }
        {
            var Q0;
            Q0=makeQuery(id+"F30.opExtrude","CAP_FACE",FACE,{"disambiguationData":[OSD([sQuery(id+"F29.wireOp",EDGE,"E90.bottom"),sQuery(id+"F29.wireOp",EDGE,"E90.top"),sQuery(id+"F29.wireOp",EDGE,"E90.left"),sQuery(id+"F29.wireOp",EDGE,"E90.right")])],"isStart":false});
            var sketch = newSketch(context, id + "F31", { "sketchPlane" : qUnion([Q0])});
            skLineSegment(sketch, "E91.bottom", {"start": v(-39.7, 19.25) * mm, "end": v(-4.7, 19.25) * mm});
            skLineSegment(sketch, "E91.top", {"start": v(-39.7, 11.75) * mm, "end": v(-4.7, 11.75) * mm});
            skLineSegment(sketch, "E91.left", {"start": v(-39.7, 19.25) * mm, "end": v(-39.7, 11.75) * mm});
            skLineSegment(sketch, "E91.right", {"start": v(-4.7, 19.25) * mm, "end": v(-4.7, 11.75) * mm});
            skSolve(sketch);
        }
        {
            var Q0;
            Q0 = qSketchRegion(id + "F31", true);
            var Q1;
            Q1=makeQuery(id+"F31.imprint","IMPRINT",FACE,{"disambiguationData":[TD([[makeQuery(id+"F31.imprint","IMPRINT",EDGE,{"derivedFrom":sQuery(id+"F31.wireOp",EDGE,"E91.bottom")}),-1.0]])]});
            extrude(context, id + "F32", {"entities" : qUnion([Q0, Q1]), "operationType" : NewBodyOperationType.ADD, "depth" : 3 * mm});
        }
        {
            var Q0;
            Q0=makeQuery(id+"F1.opExtrude","CAP_FACE",FACE,{"disambiguationData":[OSD([sQuery(id+"F0.wireOp",EDGE,"E0.bottom"),sQuery(id+"F0.wireOp",EDGE,"E0.top"),sQuery(id+"F0.wireOp",EDGE,"E0.left"),sQuery(id+"F0.wireOp",EDGE,"E0.right"),sQuery(id+"F0.wireOp",EDGE,"E1"),sQuery(id+"F0.wireOp",EDGE,"E2"),sQuery(id+"F0.wireOp",EDGE,"E3"),sQuery(id+"F0.wireOp",EDGE,"E4"),sQuery(id+"F0.wireOp",EDGE,"E5"),sQuery(id+"F0.wireOp",EDGE,"E7"),sQuery(id+"F0.wireOp",EDGE,"E9.trimOffspring"),sQuery(id+"F0.wireOp",EDGE,"E10"),sQuery(id+"F0.wireOp",EDGE,"E14")])],"isStart":true});
            var sketch = newSketch(context, id + "F33", { "sketchPlane" : qUnion([Q0])});
            skText(sketch, "E92", { "text": "Annie Zhu\nKathy Kang\n", "fontName": "OpenSans-Regular.ttf"});
            const initialGuessF33  = {"E92": [-0.03244, -0.01421, 1, 0, 0.00502]};
            skSetInitialGuess(sketch, initialGuessF33);
            skSolve(sketch);
        }
        {
            var Q0;
            Q0=makeQuery(id+"F33.imprint","IMPRINT",FACE,{"disambiguationData":[TD([[makeQuery(id+"F33.imprint","IMPRINT",EDGE,{"derivedFrom":sQuery(id+"F33.wireOp",EDGE,"E92.sketch_text.stroke-13")}),-1.0]])]});
            var Q1;
            Q1=makeQuery(id+"F33.imprint","IMPRINT",FACE,{"disambiguationData":[TD([[makeQuery(id+"F33.imprint","IMPRINT",EDGE,{"derivedFrom":sQuery(id+"F33.wireOp",EDGE,"E92.sketch_text.stroke-30")}),-1.0]])]});
            var Q2;
            Q2=makeQuery(id+"F33.imprint","IMPRINT",FACE,{"disambiguationData":[TD([[makeQuery(id+"F33.imprint","IMPRINT",EDGE,{"derivedFrom":sQuery(id+"F33.wireOp",EDGE,"E92.sketch_text.stroke-47")}),-1.0]])]});
            var Q3;
            Q3=makeQuery(id+"F33.imprint","IMPRINT",FACE,{"disambiguationData":[TD([[makeQuery(id+"F33.imprint","IMPRINT",EDGE,{"derivedFrom":sQuery(id+"F33.wireOp",EDGE,"E92.sketch_text.stroke-51")}),-1.0]])]});
            var Q4;
            Q4=makeQuery(id+"F33.imprint","IMPRINT",FACE,{"disambiguationData":[TD([[makeQuery(id+"F33.imprint","IMPRINT",EDGE,{"derivedFrom":sQuery(id+"F33.wireOp",EDGE,"E92.sketch_text.stroke-78")}),-1.0]])]});
            var Q5;
            Q5=makeQuery(id+"F33.imprint","IMPRINT",FACE,{"disambiguationData":[TD([[makeQuery(id+"F33.imprint","IMPRINT",EDGE,{"derivedFrom":sQuery(id+"F33.wireOp",EDGE,"E92.sketch_text.stroke-88")}),-1.0]])]});
            var Q6;
            Q6=makeQuery(id+"F33.imprint","IMPRINT",FACE,{"disambiguationData":[TD([[makeQuery(id+"F33.imprint","IMPRINT",EDGE,{"derivedFrom":sQuery(id+"F33.wireOp",EDGE,"E92.sketch_text.stroke-106")}),-1.0]])]});
            var Q7;
            Q7=makeQuery(id+"F33.imprint","IMPRINT",FACE,{"disambiguationData":[TD([[makeQuery(id+"F33.imprint","IMPRINT",EDGE,{"derivedFrom":sQuery(id+"F33.wireOp",EDGE,"E92.sketch_text.stroke-123")}),-1.0]])]});
            var Q8;
            Q8=makeQuery(id+"F33.imprint","IMPRINT",FACE,{"disambiguationData":[TD([[makeQuery(id+"F33.imprint","IMPRINT",EDGE,{"derivedFrom":sQuery(id+"F33.wireOp",EDGE,"E92.sketch_text.stroke-162")}),-1.0]])]});
            var Q9;
            Q9=makeQuery(id+"F33.imprint","IMPRINT",FACE,{"disambiguationData":[TD([[makeQuery(id+"F33.imprint","IMPRINT",EDGE,{"derivedFrom":sQuery(id+"F33.wireOp",EDGE,"E92.sketch_text.stroke-181")}),-1.0]])]});
            var Q10;
            Q10=makeQuery(id+"F33.imprint","IMPRINT",FACE,{"disambiguationData":[TD([[makeQuery(id+"F33.imprint","IMPRINT",EDGE,{"derivedFrom":sQuery(id+"F33.wireOp",EDGE,"E92.sketch_text.stroke-199")}),-1.0]])]});
            var Q11;
            Q11=makeQuery(id+"F33.imprint","IMPRINT",FACE,{"disambiguationData":[TD([[makeQuery(id+"F33.imprint","IMPRINT",EDGE,{"derivedFrom":sQuery(id+"F33.wireOp",EDGE,"E92.sketch_text.stroke-215")}),-1.0]])]});
            var Q12;
            Q12=makeQuery(id+"F33.imprint","IMPRINT",FACE,{"disambiguationData":[TD([[makeQuery(id+"F33.imprint","IMPRINT",EDGE,{"derivedFrom":sQuery(id+"F33.wireOp",EDGE,"E92.sketch_text.stroke-254")}),-1.0]])]});
            var Q13;
            Q13=makeQuery(id+"F33.imprint","IMPRINT",FACE,{"disambiguationData":[TD([[makeQuery(id+"F33.imprint","IMPRINT",EDGE,{"derivedFrom":sQuery(id+"F33.wireOp",EDGE,"E92.sketch_text.stroke-0")}),-1.0]])]});
            var Q14;
            Q14=makeQuery(id+"F33.imprint","IMPRINT",FACE,{"disambiguationData":[TD([[makeQuery(id+"F33.imprint","IMPRINT",EDGE,{"derivedFrom":sQuery(id+"F33.wireOp",EDGE,"E92.sketch_text.stroke-59")}),-1.0]])]});
            var Q15;
            Q15=makeQuery(id+"F33.imprint","IMPRINT",FACE,{"disambiguationData":[TD([[makeQuery(id+"F33.imprint","IMPRINT",EDGE,{"derivedFrom":sQuery(id+"F33.wireOp",EDGE,"E92.sketch_text.stroke-135")}),-1.0]])]});
            var Q16;
            Q16=makeQuery(id+"F33.imprint","IMPRINT",FACE,{"disambiguationData":[TD([[makeQuery(id+"F33.imprint","IMPRINT",EDGE,{"derivedFrom":sQuery(id+"F33.wireOp",EDGE,"E92.sketch_text.stroke-227")}),-1.0]])]});
            var Q17;
            Q17=makeQuery(id+"F33.imprint","IMPRINT",FACE,{"disambiguationData":[TD([[makeQuery(id+"F33.imprint","IMPRINT",EDGE,{"derivedFrom":sQuery(id+"F33.wireOp",EDGE,"E92.sketch_text.stroke-271")}),-1.0]])]});
            extrude(context, id + "F34", {"entities" : qUnion([Q0, Q1, Q2, Q3, Q4, Q5, Q6, Q7, Q8, Q9, Q10, Q11, Q12, Q13, Q14, Q15, Q16, Q17]), "operationType" : NewBodyOperationType.ADD, "depth" : 0.5 * mm});
        }
    });